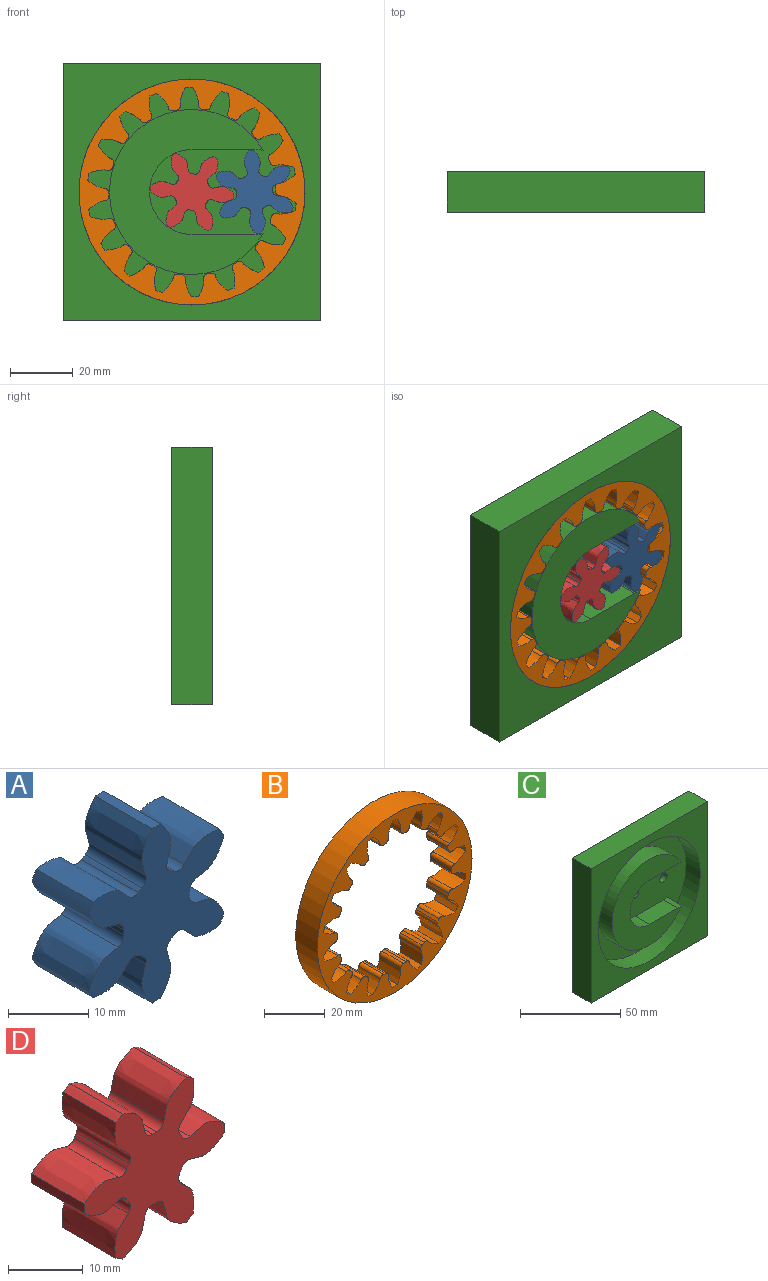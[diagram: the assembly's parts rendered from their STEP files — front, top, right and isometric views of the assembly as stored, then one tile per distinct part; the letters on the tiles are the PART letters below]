
ASSEMBLY  parts=4 mates=3
PART A: 38 faces, bbox 23.7x10x26.6 mm
  f0: cylinder r=13.28mm len=10mm, axis (0,1,0), area 15.2mm2, adj f5,f7,f23,f35
  f1: cylinder r=13.28mm len=10mm, axis (0,1,0), area 15.2mm2, adj f5,f7,f30,f33
  f2: cylinder r=13.28mm len=10mm, axis (0,1,0), area 15.2mm2, adj f5,f7,f18,f25
  f3: cylinder r=13.28mm len=10mm, axis (0,1,0), area 15.2mm2, adj f5,f7,f8,f20
  f4: cylinder r=13.28mm len=10mm, axis (0,1,0), area 15.2mm2, adj f5,f7,f15,f28
  f5: plane 26.57x23.73mm, normal (0,-1,0), area 290.5mm2, adj f0,f1,f2,f3,f4,f6,f8,f9
  f6: cylinder r=13.28mm len=10mm, axis (0,1,0), area 15.2mm2, adj f5,f7,f10,f13
  f7: plane 26.57x23.73mm, normal (0,1,0), area 290.5mm2, adj f0,f1,f2,f3,f4,f6,f8,f9
  f8: extruded ~10x5.11mm, area 70.7mm2, adj f3,f5,f7,f11
  f9: cylinder r=5.78mm len=10mm, axis (0,1,0), area 7.9mm2, adj f5,f7,f11,f12
  f10: extruded ~10x5.11mm, area 70.7mm2, adj f5,f6,f7,f12
  f11: cylinder r=1.31mm len=10mm, axis (0,1,0), area 18.2mm2, adj f5,f7,f8,f9
  f12: cylinder r=1.31mm len=10mm, axis (0,1,0), area 18.2mm2, adj f5,f7,f9,f10
  f13: extruded ~10x6.21mm, area 70.7mm2, adj f5,f6,f7,f16
  f14: cylinder r=5.78mm len=10mm, axis (0,1,0), area 7.9mm2, adj f5,f7,f16,f17
  f15: extruded ~10x6.54mm, area 70.7mm2, adj f4,f5,f7,f17
  f16: cylinder r=1.31mm len=10mm, axis (0,1,0), area 18.2mm2, adj f5,f7,f13,f14
  f17: cylinder r=1.31mm len=10mm, axis (0,1,0), area 18.2mm2, adj f5,f7,f14,f15
  f18: extruded ~10x6.54mm, area 70.7mm2, adj f2,f5,f7,f21
  f19: cylinder r=5.78mm len=10mm, axis (0,1,0), area 7.9mm2, adj f5,f7,f21,f22
  f20: extruded ~10x6.21mm, area 70.7mm2, adj f3,f5,f7,f22
  f21: cylinder r=1.31mm len=10mm, axis (0,1,0), area 18.2mm2, adj f5,f7,f18,f19
  f22: cylinder r=1.31mm len=10mm, axis (0,1,0), area 18.2mm2, adj f5,f7,f19,f20
  f23: extruded ~10x6.21mm, area 70.7mm2, adj f0,f5,f7,f26
  f24: cylinder r=5.78mm len=10mm, axis (0,1,0), area 7.9mm2, adj f5,f7,f26,f27
  f25: extruded ~10x6.54mm, area 70.7mm2, adj f2,f5,f7,f27
  f26: cylinder r=1.31mm len=10mm, axis (0,1,0), area 18.2mm2, adj f5,f7,f23,f24
  f27: cylinder r=1.31mm len=10mm, axis (0,1,0), area 18.2mm2, adj f5,f7,f24,f25
  f28: extruded ~10x6.54mm, area 70.7mm2, adj f4,f5,f7,f31
  f29: cylinder r=5.78mm len=10mm, axis (0,1,0), area 7.9mm2, adj f5,f7,f31,f32
  f30: extruded ~10x6.21mm, area 70.7mm2, adj f1,f5,f7,f32
  f31: cylinder r=1.31mm len=10mm, axis (0,1,0), area 18.2mm2, adj f5,f7,f28,f29
  f32: cylinder r=1.31mm len=10mm, axis (0,1,0), area 18.2mm2, adj f5,f7,f29,f30
  f33: extruded ~10x5.11mm, area 70.7mm2, adj f1,f5,f7,f36
  f34: cylinder r=5.78mm len=10mm, axis (0,1,0), area 7.9mm2, adj f5,f7,f36,f37
  f35: extruded ~10x5.11mm, area 70.7mm2, adj f0,f5,f7,f37
  f36: cylinder r=1.31mm len=10mm, axis (0,1,0), area 18.2mm2, adj f5,f7,f33,f34
  f37: cylinder r=1.31mm len=10mm, axis (0,1,0), area 18.2mm2, adj f5,f7,f34,f35
PART B: 111 faces, bbox 72x10x72 mm
  f0: plane 72x72mm, normal (0,-1,0), area 1245.9mm2, adj f2,f3,f4,f5,f6,f7,f8,f9
  f1: plane 72x72mm, normal (0,1,0), area 1245.9mm2, adj f2,f3,f4,f5,f6,f7,f8,f9
  f2: cylinder r=36mm len=72mm, axis (0,1,0), area 2261.9mm2, adj f0,f1
  f3: cylinder r=33.38mm len=10mm, axis (0,1,0), area 23.3mm2, adj f0,f1,f101,f108
  f4: cylinder r=33.38mm len=10mm, axis (0,1,0), area 23.3mm2, adj f0,f1,f96,f103
  f5: cylinder r=33.38mm len=10mm, axis (0,1,0), area 23.3mm2, adj f0,f1,f91,f98
  f6: cylinder r=33.38mm len=10mm, axis (0,1,0), area 23.3mm2, adj f0,f1,f21,f93
  f7: cylinder r=33.38mm len=10mm, axis (0,1,0), area 23.3mm2, adj f0,f1,f81,f88
  f8: cylinder r=33.38mm len=10mm, axis (0,1,0), area 23.3mm2, adj f0,f1,f76,f83
  f9: cylinder r=33.38mm len=10mm, axis (0,1,0), area 23.3mm2, adj f0,f1,f71,f78
  f10: cylinder r=33.38mm len=10mm, axis (0,1,0), area 23.3mm2, adj f0,f1,f73,f106
  f11: cylinder r=33.38mm len=10mm, axis (0,1,0), area 23.3mm2, adj f0,f1,f68,f86
  f12: cylinder r=33.38mm len=10mm, axis (0,1,0), area 23.3mm2, adj f0,f1,f63,f66
  f13: cylinder r=33.38mm len=10mm, axis (0,1,0), area 23.3mm2, adj f0,f1,f51,f58
  f14: cylinder r=33.38mm len=10mm, axis (0,1,0), area 23.3mm2, adj f0,f1,f53,f61
  f15: cylinder r=33.38mm len=10mm, axis (0,1,0), area 23.3mm2, adj f0,f1,f48,f56
  f16: cylinder r=33.38mm len=10mm, axis (0,1,0), area 23.3mm2, adj f0,f1,f43,f46
  f17: cylinder r=33.38mm len=10mm, axis (0,1,0), area 23.3mm2, adj f0,f1,f31,f38
  f18: cylinder r=33.38mm len=10mm, axis (0,1,0), area 23.3mm2, adj f0,f1,f33,f41
  f19: cylinder r=33.38mm len=10mm, axis (0,1,0), area 23.3mm2, adj f0,f1,f28,f36
  f20: cylinder r=33.38mm len=10mm, axis (0,1,0), area 23.3mm2, adj f0,f1,f23,f26
  f21: extruded ~10x5.28mm, area 60.1mm2, adj f0,f1,f6,f24
  f22: cylinder r=26.55mm len=10mm, axis (0,1,0), area 11.9mm2, adj f0,f1,f24,f25
  f23: extruded ~10x5.28mm, area 60.1mm2, adj f0,f1,f20,f25
  f24: cylinder r=1.34mm len=10mm, axis (0,1,0), area 20.3mm2, adj f0,f1,f21,f22
  f25: cylinder r=1.34mm len=10mm, axis (0,1,0), area 20.3mm2, adj f0,f1,f22,f23
  f26: extruded ~10x5.88mm, area 60.1mm2, adj f0,f1,f20,f29
  f27: cylinder r=26.55mm len=10mm, axis (0,1,0), area 11.9mm2, adj f0,f1,f29,f30
  f28: extruded ~10x4.33mm, area 60.1mm2, adj f0,f1,f19,f30
  f29: cylinder r=1.34mm len=10mm, axis (0,1,0), area 20.3mm2, adj f0,f1,f26,f27
  f30: cylinder r=1.34mm len=10mm, axis (0,1,0), area 20.3mm2, adj f0,f1,f27,f28
  f31: extruded ~10x4.97mm, area 60.1mm2, adj f0,f1,f17,f34
  f32: cylinder r=26.55mm len=10mm, axis (0,1,0), area 11.9mm2, adj f0,f1,f34,f35
  f33: extruded ~10x5.91mm, area 60.1mm2, adj f0,f1,f18,f35
  f34: cylinder r=1.34mm len=10mm, axis (0,1,0), area 20.3mm2, adj f0,f1,f31,f32
  f35: cylinder r=1.34mm len=10mm, axis (0,1,0), area 20.3mm2, adj f0,f1,f32,f33
  f36: extruded ~10x5.77mm, area 60.1mm2, adj f0,f1,f19,f39
  f37: cylinder r=26.55mm len=10mm, axis (0,1,0), area 11.9mm2, adj f0,f1,f39,f40
  f38: extruded ~10x5.45mm, area 60.1mm2, adj f0,f1,f17,f40
  f39: cylinder r=1.34mm len=10mm, axis (0,1,0), area 20.3mm2, adj f0,f1,f36,f37
  f40: cylinder r=1.34mm len=10mm, axis (0,1,0), area 20.3mm2, adj f0,f1,f37,f38
  f41: extruded ~10x4.73mm, area 60.1mm2, adj f0,f1,f18,f44
  f42: cylinder r=26.55mm len=10mm, axis (0,1,0), area 11.9mm2, adj f0,f1,f44,f45
  f43: extruded ~10x5.66mm, area 60.1mm2, adj f0,f1,f16,f45
  f44: cylinder r=1.34mm len=10mm, axis (0,1,0), area 20.3mm2, adj f0,f1,f41,f42
  f45: cylinder r=1.34mm len=10mm, axis (0,1,0), area 20.3mm2, adj f0,f1,f42,f43
  f46: extruded ~10x5.66mm, area 60.1mm2, adj f0,f1,f16,f49
  f47: cylinder r=26.55mm len=10mm, axis (0,1,0), area 11.9mm2, adj f0,f1,f49,f50
  f48: extruded ~10x4.73mm, area 60.1mm2, adj f0,f1,f15,f50
  f49: cylinder r=1.34mm len=10mm, axis (0,1,0), area 20.3mm2, adj f0,f1,f46,f47
  f50: cylinder r=1.34mm len=10mm, axis (0,1,0), area 20.3mm2, adj f0,f1,f47,f48
  f51: extruded ~10x5.45mm, area 60.1mm2, adj f0,f1,f13,f54
  f52: cylinder r=26.55mm len=10mm, axis (0,1,0), area 11.9mm2, adj f0,f1,f54,f55
  f53: extruded ~10x5.77mm, area 60.1mm2, adj f0,f1,f14,f55
  f54: cylinder r=1.34mm len=10mm, axis (0,1,0), area 20.3mm2, adj f0,f1,f51,f52
  f55: cylinder r=1.34mm len=10mm, axis (0,1,0), area 20.3mm2, adj f0,f1,f52,f53
  f56: extruded ~10x5.91mm, area 60.1mm2, adj f0,f1,f15,f59
  f57: cylinder r=26.55mm len=10mm, axis (0,1,0), area 11.9mm2, adj f0,f1,f59,f60
  f58: extruded ~10x4.97mm, area 60.1mm2, adj f0,f1,f13,f60
  f59: cylinder r=1.34mm len=10mm, axis (0,1,0), area 20.3mm2, adj f0,f1,f56,f57
  f60: cylinder r=1.34mm len=10mm, axis (0,1,0), area 20.3mm2, adj f0,f1,f57,f58
  f61: extruded ~10x4.33mm, area 60.1mm2, adj f0,f1,f14,f64
  f62: cylinder r=26.55mm len=10mm, axis (0,1,0), area 11.9mm2, adj f0,f1,f64,f65
  f63: extruded ~10x5.88mm, area 60.1mm2, adj f0,f1,f12,f65
  f64: cylinder r=1.34mm len=10mm, axis (0,1,0), area 20.3mm2, adj f0,f1,f61,f62
  f65: cylinder r=1.34mm len=10mm, axis (0,1,0), area 20.3mm2, adj f0,f1,f62,f63
  f66: extruded ~10x5.28mm, area 60.1mm2, adj f0,f1,f12,f69
  f67: cylinder r=26.55mm len=10mm, axis (0,1,0), area 11.9mm2, adj f0,f1,f69,f70
  f68: extruded ~10x5.28mm, area 60.1mm2, adj f0,f1,f11,f70
  f69: cylinder r=1.34mm len=10mm, axis (0,1,0), area 20.3mm2, adj f0,f1,f66,f67
  f70: cylinder r=1.34mm len=10mm, axis (0,1,0), area 20.3mm2, adj f0,f1,f67,f68
  f71: extruded ~10x4.73mm, area 60.1mm2, adj f0,f1,f9,f74
  f72: cylinder r=26.55mm len=10mm, axis (0,1,0), area 11.9mm2, adj f0,f1,f74,f75
  f73: extruded ~10x5.66mm, area 60.1mm2, adj f0,f1,f10,f75
  f74: cylinder r=1.34mm len=10mm, axis (0,1,0), area 20.3mm2, adj f0,f1,f71,f72
  f75: cylinder r=1.34mm len=10mm, axis (0,1,0), area 20.3mm2, adj f0,f1,f72,f73
  f76: extruded ~10x4.97mm, area 60.1mm2, adj f0,f1,f8,f79
  f77: cylinder r=26.55mm len=10mm, axis (0,1,0), area 11.9mm2, adj f0,f1,f79,f80
  f78: extruded ~10x5.91mm, area 60.1mm2, adj f0,f1,f9,f80
  f79: cylinder r=1.34mm len=10mm, axis (0,1,0), area 20.3mm2, adj f0,f1,f76,f77
  f80: cylinder r=1.34mm len=10mm, axis (0,1,0), area 20.3mm2, adj f0,f1,f77,f78
  f81: extruded ~10x5.77mm, area 60.1mm2, adj f0,f1,f7,f84
  f82: cylinder r=26.55mm len=10mm, axis (0,1,0), area 11.9mm2, adj f0,f1,f84,f85
  f83: extruded ~10x5.45mm, area 60.1mm2, adj f0,f1,f8,f85
  f84: cylinder r=1.34mm len=10mm, axis (0,1,0), area 20.3mm2, adj f0,f1,f81,f82
  f85: cylinder r=1.34mm len=10mm, axis (0,1,0), area 20.3mm2, adj f0,f1,f82,f83
  f86: extruded ~10x5.88mm, area 60.1mm2, adj f0,f1,f11,f89
  f87: cylinder r=26.55mm len=10mm, axis (0,1,0), area 11.9mm2, adj f0,f1,f89,f90
  f88: extruded ~10x4.33mm, area 60.1mm2, adj f0,f1,f7,f90
  f89: cylinder r=1.34mm len=10mm, axis (0,1,0), area 20.3mm2, adj f0,f1,f86,f87
  f90: cylinder r=1.34mm len=10mm, axis (0,1,0), area 20.3mm2, adj f0,f1,f87,f88
  f91: extruded ~10x4.33mm, area 60.1mm2, adj f0,f1,f5,f94
  f92: cylinder r=26.55mm len=10mm, axis (0,1,0), area 11.9mm2, adj f0,f1,f94,f95
  f93: extruded ~10x5.88mm, area 60.1mm2, adj f0,f1,f6,f95
  f94: cylinder r=1.34mm len=10mm, axis (0,1,0), area 20.3mm2, adj f0,f1,f91,f92
  f95: cylinder r=1.34mm len=10mm, axis (0,1,0), area 20.3mm2, adj f0,f1,f92,f93
  f96: extruded ~10x5.45mm, area 60.1mm2, adj f0,f1,f4,f99
  f97: cylinder r=26.55mm len=10mm, axis (0,1,0), area 11.9mm2, adj f0,f1,f99,f100
  f98: extruded ~10x5.77mm, area 60.1mm2, adj f0,f1,f5,f100
  f99: cylinder r=1.34mm len=10mm, axis (0,1,0), area 20.3mm2, adj f0,f1,f96,f97
  f100: cylinder r=1.34mm len=10mm, axis (0,1,0), area 20.3mm2, adj f0,f1,f97,f98
  f101: extruded ~10x5.91mm, area 60.1mm2, adj f0,f1,f3,f104
  f102: cylinder r=26.55mm len=10mm, axis (0,1,0), area 11.9mm2, adj f0,f1,f104,f105
  f103: extruded ~10x4.97mm, area 60.1mm2, adj f0,f1,f4,f105
  f104: cylinder r=1.34mm len=10mm, axis (0,1,0), area 20.3mm2, adj f0,f1,f101,f102
  f105: cylinder r=1.34mm len=10mm, axis (0,1,0), area 20.3mm2, adj f0,f1,f102,f103
  f106: extruded ~10x5.66mm, area 60.1mm2, adj f0,f1,f10,f109
  f107: cylinder r=26.55mm len=10mm, axis (0,1,0), area 11.9mm2, adj f0,f1,f109,f110
  f108: extruded ~10x4.73mm, area 60.1mm2, adj f0,f1,f3,f110
  f109: cylinder r=1.34mm len=10mm, axis (0,1,0), area 20.3mm2, adj f0,f1,f106,f107
  f110: cylinder r=1.34mm len=10mm, axis (0,1,0), area 20.3mm2, adj f0,f1,f107,f108
PART C: 17 faces, bbox 82x13x82 mm
  f0: plane 82x13mm, normal (0,0,-1), area 1066mm2, adj f1,f4,f5,f14
  f1: plane 82x13mm, normal (1,0,0), area 1066mm2, adj f0,f2,f5,f14
  f2: plane 82x13mm, normal (0,0,1), area 1066mm2, adj f1,f4,f5,f14
  f3: cylinder r=36mm len=72mm, axis (0,1,0), area 2261.9mm2, adj f5,f13
  f4: plane 82x13mm, normal (-1,0,0), area 1066mm2, adj f0,f2,f5,f14
  f5: plane 82x82mm, normal (0,-1,0), area 2652.5mm2, adj f0,f1,f2,f3,f4
  f6: plane 52.5x48.92mm, normal (0,-1,0), area 1202.8mm2, adj f7,f8,f9,f10,f11,f12
  f7: cylinder r=26.25mm len=52.5mm, axis (0,1,0), area 1371.9mm2, adj f6,f8,f12,f13
  f8: cylinder r=13.5mm len=10mm, axis (0,1,0), area 26.9mm2, adj f6,f7,f9,f13
  f9: plane 20x10mm, normal (0,0,-1), area 200mm2, adj f6,f8,f10,f13
  f10: cylinder r=13.5mm len=27mm, axis (0,1,0), area 424.1mm2, adj f6,f9,f11,f13
  f11: plane 20x10mm, normal (0,0,1), area 200mm2, adj f6,f10,f12,f13
  f12: cylinder r=13.5mm len=10mm, axis (0,1,0), area 26.9mm2, adj f6,f7,f11,f13
  f13: plane 72x72mm, normal (0,-1,0), area 2824.6mm2, adj f3,f7,f8,f9,f10,f11,f12,f15
  f14: plane 82x82mm, normal (0,1,0), area 6679.9mm2, adj f0,f1,f2,f4,f15,f16
  f15: cylinder r=2.65mm len=5.3mm, axis (0,-1,0), area 50mm2, adj f13,f14
  f16: cylinder r=2.65mm len=5.3mm, axis (0,-1,0), area 50mm2, adj f13,f14
PART D: 38 faces, bbox 26.6x10x23.7 mm
  f0: cylinder r=13.28mm len=10mm, axis (0,1,0), area 15.2mm2, adj f5,f7,f30,f34
  f1: cylinder r=13.28mm len=10mm, axis (0,1,0), area 15.2mm2, adj f5,f7,f10,f29
  f2: cylinder r=13.28mm len=10mm, axis (0,1,0), area 15.2mm2, adj f5,f7,f20,f24
  f3: cylinder r=13.28mm len=10mm, axis (0,1,0), area 15.2mm2, adj f5,f7,f19,f35
  f4: cylinder r=13.28mm len=10mm, axis (0,1,0), area 15.2mm2, adj f5,f7,f14,f25
  f5: plane 26.57x23.73mm, normal (0,-1,0), area 290.5mm2, adj f0,f1,f2,f3,f4,f6,f8,f9
  f6: cylinder r=13.28mm len=10mm, axis (0,1,0), area 15.2mm2, adj f5,f7,f9,f15
  f7: plane 26.57x23.73mm, normal (0,1,0), area 290.5mm2, adj f0,f1,f2,f3,f4,f6,f8,f9
  f8: cylinder r=5.78mm len=10mm, axis (0,1,0), area 7.9mm2, adj f5,f7,f11,f12
  f9: extruded ~10x6.54mm, area 70.7mm2, adj f5,f6,f7,f11
  f10: extruded ~10x6.21mm, area 70.7mm2, adj f1,f5,f7,f12
  f11: cylinder r=1.31mm len=10mm, axis (0,1,0), area 18.2mm2, adj f5,f7,f8,f9
  f12: cylinder r=1.31mm len=10mm, axis (0,1,0), area 18.2mm2, adj f5,f7,f8,f10
  f13: cylinder r=5.78mm len=10mm, axis (0,1,0), area 7.9mm2, adj f5,f7,f16,f17
  f14: extruded ~10x6.21mm, area 70.7mm2, adj f4,f5,f7,f16
  f15: extruded ~10x6.54mm, area 70.7mm2, adj f5,f6,f7,f17
  f16: cylinder r=1.31mm len=10mm, axis (0,1,0), area 18.2mm2, adj f5,f7,f13,f14
  f17: cylinder r=1.31mm len=10mm, axis (0,1,0), area 18.2mm2, adj f5,f7,f13,f15
  f18: cylinder r=5.78mm len=10mm, axis (0,1,0), area 7.9mm2, adj f5,f7,f21,f22
  f19: extruded ~10x6.54mm, area 70.7mm2, adj f3,f5,f7,f21
  f20: extruded ~10x6.21mm, area 70.7mm2, adj f2,f5,f7,f22
  f21: cylinder r=1.31mm len=10mm, axis (0,1,0), area 18.2mm2, adj f5,f7,f18,f19
  f22: cylinder r=1.31mm len=10mm, axis (0,1,0), area 18.2mm2, adj f5,f7,f18,f20
  f23: cylinder r=5.78mm len=10mm, axis (0,1,0), area 7.9mm2, adj f5,f7,f26,f27
  f24: extruded ~10x5.11mm, area 70.7mm2, adj f2,f5,f7,f26
  f25: extruded ~10x5.11mm, area 70.7mm2, adj f4,f5,f7,f27
  f26: cylinder r=1.31mm len=10mm, axis (0,1,0), area 18.2mm2, adj f5,f7,f23,f24
  f27: cylinder r=1.31mm len=10mm, axis (0,1,0), area 18.2mm2, adj f5,f7,f23,f25
  f28: cylinder r=5.78mm len=10mm, axis (0,1,0), area 7.9mm2, adj f5,f7,f31,f32
  f29: extruded ~10x5.11mm, area 70.7mm2, adj f1,f5,f7,f31
  f30: extruded ~10x5.11mm, area 70.7mm2, adj f0,f5,f7,f32
  f31: cylinder r=1.31mm len=10mm, axis (0,1,0), area 18.2mm2, adj f5,f7,f28,f29
  f32: cylinder r=1.31mm len=10mm, axis (0,1,0), area 18.2mm2, adj f5,f7,f28,f30
  f33: cylinder r=5.78mm len=10mm, axis (0,1,0), area 7.9mm2, adj f5,f7,f36,f37
  f34: extruded ~10x6.21mm, area 70.7mm2, adj f0,f5,f7,f36
  f35: extruded ~10x6.54mm, area 70.7mm2, adj f3,f5,f7,f37
  f36: cylinder r=1.31mm len=10mm, axis (0,1,0), area 18.2mm2, adj f5,f7,f33,f34
  f37: cylinder r=1.31mm len=10mm, axis (0,1,0), area 18.2mm2, adj f5,f7,f33,f35
PLACE A rot(axis=(-0.46,0,-0.89),180deg) t=(77.44,34.65,-2.04)mm
PLACE B rot(axis=(0.16,0,0.99),180deg) t=(45.97,34.65,14.34)mm
PLACE C t=(45.97,44.65,14.34)mm fixed
PLACE D rot(axis=(-0.46,0,0.89),180deg) t=(45.97,34.65,14.34)mm
MATE revolute A.f0 <-> C.f16  axis (0,1,0) through (65.97,44.65,14.34)mm
MATE revolute D.f0 <-> C.f3  axis (0,1,0) through (45.97,44.65,14.34)mm
MATE revolute B.f2 <-> C.f3  axis (0,1,0) through (45.97,44.65,14.34)mm
